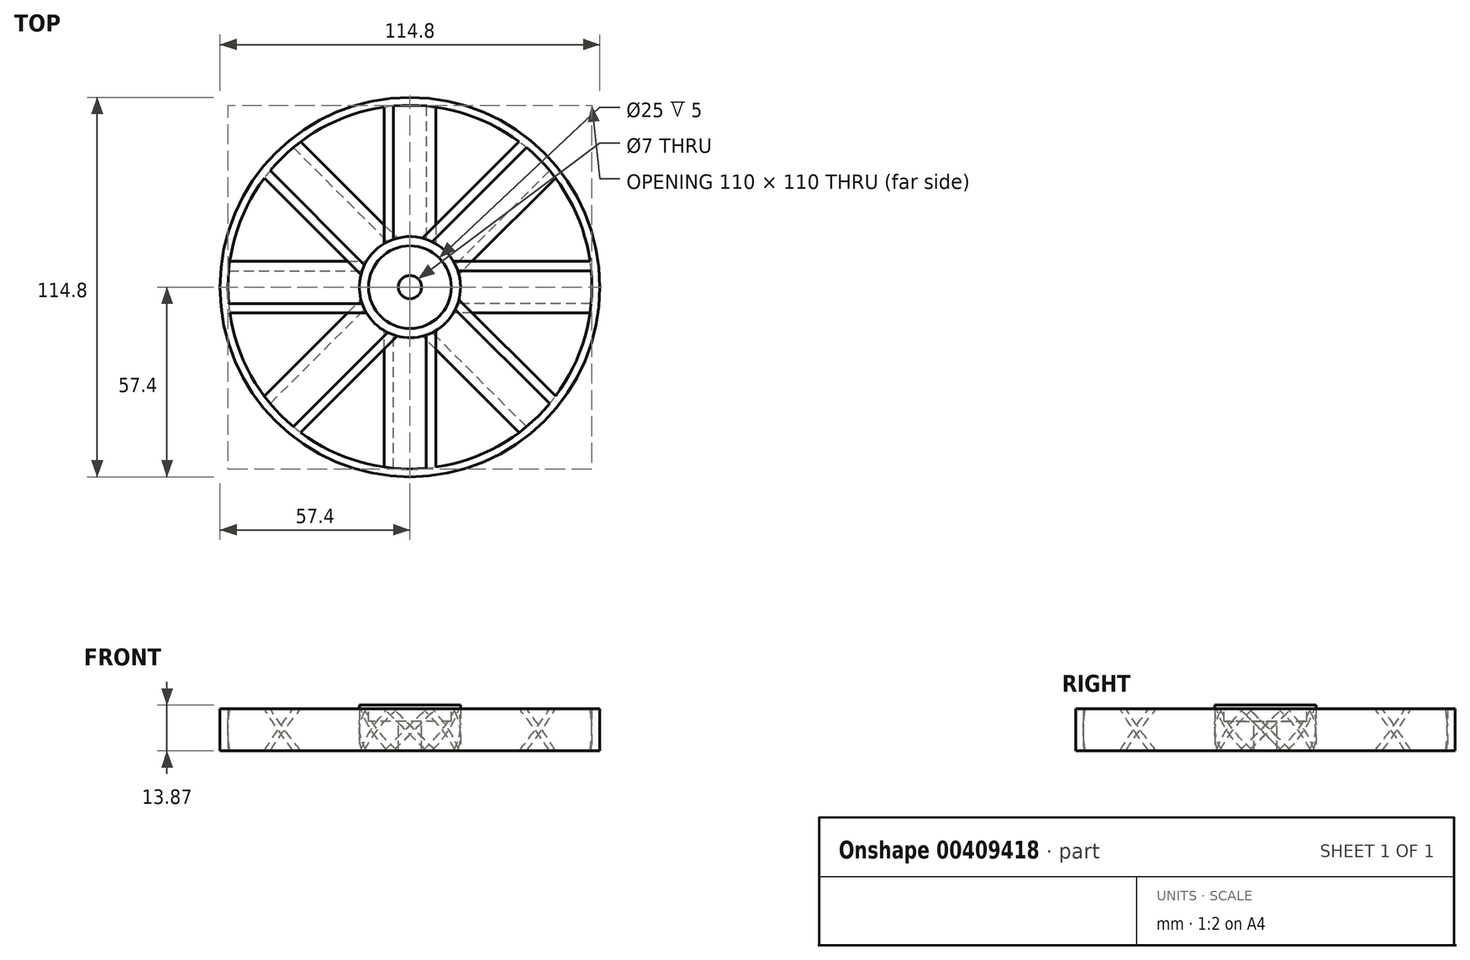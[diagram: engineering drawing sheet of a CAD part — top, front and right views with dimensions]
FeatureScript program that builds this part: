
annotation { "Feature Type Name" : "Feature", "Feature Type Description" : "" }
export const myFeature = defineFeature(function(context is Context, id is Id, definition is map)
    precondition{}
    {
        {
            var Q0;
            Q0=qCreatedBy(makeId("Top.planeOp"),FACE);
            var sketch = newSketch(context, id + "F0", { "sketchPlane" : qUnion([Q0])});
            skCircle(sketch, "E0", {"center": v(0, 0) * mm, "radius": 15.29 * mm});
            skSolve(sketch);
        }
        {
            var Q0;
            Q0 = qSketchRegion(id + "F0", true);
            extrude(context, id + "F1", {"entities" : qUnion([Q0]), "depth" : 15 * mm, "offsetDistance" : 25 * mm, "symmetric" : true});
        }
        {
            var Q0;
            Q0=qCreatedBy(makeId("Right.planeOp"),FACE);
            cPlane(context, id + "F2", {"entities" : qUnion([Q0]), "cplaneType" : CPlaneType.OFFSET, "offset" : 10 * mm, "width" : 150 * mm, "height" : 150 * mm});
        }
        {
            var Q0;
            Q0=qCreatedBy(id+"F2.planeOp",FACE);
            var sketch = newSketch(context, id + "F3", { "sketchPlane" : qUnion([Q0])});
            skLineSegment(sketch, "E1.0", {"start": v(-0.7, 0.7) * mm, "end": v(4.95, 6.36) * mm});
            skLineSegment(sketch, "E1.1", {"start": v(-0.7, 0.7) * mm, "end": v(-7.78, -6.36) * mm});
            skLineSegment(sketch, "E2.0", {"start": v(0.7, -0.7) * mm, "end": v(7.78, 6.36) * mm});
            skLineSegment(sketch, "E2.1", {"start": v(0.7, -0.7) * mm, "end": v(-4.95, -6.36) * mm});
            skLineSegment(sketch, "E3", {"start": v(7.78, 6.36) * mm, "end": v(4.95, 6.36) * mm});
            skLineSegment(sketch, "E4", {"start": v(-7.78, -6.36) * mm, "end": v(-4.95, -6.36) * mm});
            skSolve(sketch);
        }
        {
            var Q0;
            Q0 = qSketchRegion(id + "F3", true);
            extrude(context, id + "F4", {"entities" : qUnion([Q0]), "operationType" : NewBodyOperationType.ADD, "depth" : 45 * mm, "offsetDistance" : 25 * mm});
        }
        {
            var Q0;
            Q0=makeQuery(id+"F1.opExtrude","SWEPT_BODY",BODY,{"disambiguationData":[OSD([sQuery(id+"F0.wireOp",EDGE,"E0")])]});
            var Q1;
            Q1=makeQuery(id+"F1.opExtrude","CAP_EDGE",EDGE,{"disambiguationData":[OSD([sQuery(id+"F0.wireOp",EDGE,"E0")])],"isStart":false});
            circularPattern(context, id + "F5", {"entities" : qUnion([Q0]), "axis" : qUnion([Q1]), "angle" : 360 * degree, "instanceCount" : 8, "equalSpace" : true, "isCentered" : true, "computeTransformsWithoutBuiltin" : true});
        }
        {
            var Q0;
            Q0=makeQuery(id+"F1.opExtrude","CAP_FACE",FACE,{"disambiguationData":[OSD([sQuery(id+"F0.wireOp",EDGE,"E0")])],"isStart":false});
            var sketch = newSketch(context, id + "F6", { "sketchPlane" : qUnion([Q0])});
            skCircle(sketch, "E5", {"center": v(0, 0) * mm, "radius": 9.5 * mm});
            skSolve(sketch);
        }
        {
            var Q0;
            Q0=makeQuery(id+"F6.imprint","IMPRINT",FACE,{"disambiguationData":[TD([[makeQuery(id+"F6.imprint","IMPRINT",EDGE,{"derivedFrom":sQuery(id+"F6.wireOp",EDGE,"E5")}),1.0]])]});
            var sketch = newSketch(context, id + "F7", { "sketchPlane" : qUnion([Q0])});
            skCircle(sketch, "E6", {"center": v(0, 0) * mm, "radius": 12.5 * mm});
            skSolve(sketch);
        }
        {
            var Q0;
            Q0 = qSketchRegion(id + "F7", true);
            extrude(context, id + "F8", {"entities" : qUnion([Q0]), "operationType" : NewBodyOperationType.REMOVE, "oppositeDirection" : true, "depth" : 5 * mm, "offsetDistance" : 25 * mm});
        }
        {
            var Q0;
            Q0=makeQuery(id+"F6.imprint","IMPRINT",FACE,{"disambiguationData":[TD([[makeQuery(id+"F6.imprint","IMPRINT",EDGE,{"derivedFrom":sQuery(id+"F6.wireOp",EDGE,"E5")}),1.0]])]});
            var sketch = newSketch(context, id + "F9", { "sketchPlane" : qUnion([Q0])});
            skCircle(sketch, "E7", {"center": v(0, 0) * mm, "radius": 9.5 * mm});
            skSolve(sketch);
        }
        {
            var Q0;
            Q0=qCreatedBy(makeId("Right.planeOp"),FACE);
            var sketch = newSketch(context, id + "F10", { "sketchPlane" : qUnion([Q0])});
            skLineSegment(sketch, "E8.0", {"start": v(-42.4, -6.36) * mm, "end": v(-13.73, -6.36) * mm});
            skLineSegment(sketch, "E9", {"start": v(-16.84, -6.36) * mm, "end": v(18.7, -6.36) * mm});
            skLineSegment(sketch, "E10", {"start": v(18.7, -6.36) * mm, "end": v(18.7, -12.86) * mm});
            skLineSegment(sketch, "E11", {"start": v(18.7, -12.86) * mm, "end": v(-16.84, -12.86) * mm});
            skLineSegment(sketch, "E12", {"start": v(-16.84, -12.86) * mm, "end": v(-16.84, -6.36) * mm});
            skSolve(sketch);
        }
        {
            var Q0;
            Q0 = qSketchRegion(id + "F10", true);
            extrude(context, id + "F11", {"entities" : qUnion([Q0]), "operationType" : NewBodyOperationType.REMOVE, "oppositeDirection" : true, "depth" : 40 * mm, "offsetDistance" : 25 * mm, "symmetric" : true});
        }
        {
            var Q0;
            Q0=makeQuery(id+"F9.imprint","IMPRINT",FACE,{"disambiguationData":[TD([[makeQuery(id+"F9.imprint","IMPRINT",EDGE,{"derivedFrom":sQuery(id+"F9.wireOp",EDGE,"E7")}),1.0]])]});
            var sketch = newSketch(context, id + "F12", { "sketchPlane" : qUnion([Q0])});
            skCircle(sketch, "E13", {"center": v(0, 0) * mm, "radius": 3.5 * mm});
            skSolve(sketch);
        }
        {
            var Q0;
            Q0 = qSketchRegion(id + "F12", true);
            extrude(context, id + "F13", {"entities" : qUnion([Q0]), "operationType" : NewBodyOperationType.REMOVE, "endBound" : BoundingType.THROUGH_ALL, "oppositeDirection" : true, "depth" : 25 * mm, "offsetDistance" : 25 * mm});
        }
        {
            var Q0;
            Q0=qCreatedBy(makeId("Top.planeOp"),FACE);
            var sketch = newSketch(context, id + "F14", { "sketchPlane" : qUnion([Q0])});
            skCircle(sketch, "E14", {"center": v(0, 0) * mm, "radius": 55 * mm});
            skCircle(sketch, "E15.0", {"center": v(0, 0) * mm, "radius": 57.4 * mm});
            skSolve(sketch);
        }
        {
            var Q0;
            Q0 = qSketchRegion(id + "F14", true);
            extrude(context, id + "F15", {"entities" : qUnion([Q0]), "operationType" : NewBodyOperationType.ADD, "depth" : 12.73 * mm, "offsetDistance" : 25 * mm, "symmetric" : true});
        }
    });
